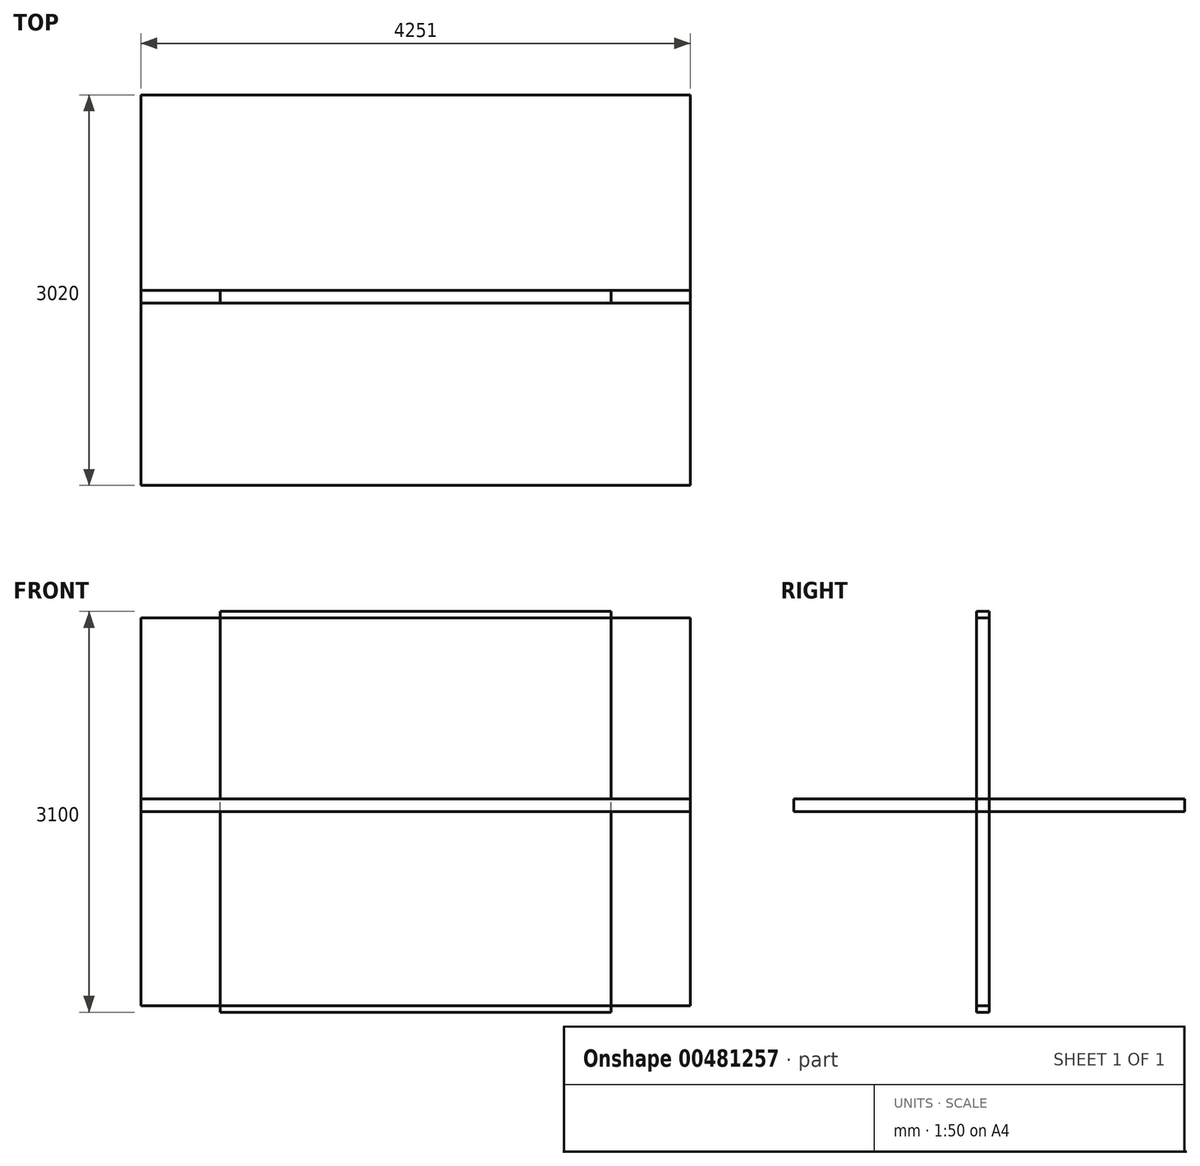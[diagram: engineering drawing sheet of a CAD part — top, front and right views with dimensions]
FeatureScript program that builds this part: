
annotation { "Feature Type Name" : "Feature", "Feature Type Description" : "" }
export const myFeature = defineFeature(function(context is Context, id is Id, definition is map)
    precondition{}
    {
        {
            var Q0;
            Q0=qCreatedBy(makeId("Front.planeOp"),FACE);
            var sketch = newSketch(context, id + "F0", { "sketchPlane" : qUnion([Q0])});
            skLineSegment(sketch, "E0.bottom", {"start": v(2125.5, -1500) * mm, "end": v(-2125.5, -1500) * mm});
            skLineSegment(sketch, "E0.top", {"start": v(2125.5, 1500) * mm, "end": v(-2125.5, 1500) * mm});
            skLineSegment(sketch, "E0.left", {"start": v(2125.5, -1500) * mm, "end": v(2125.5, 1500) * mm});
            skLineSegment(sketch, "E0.right", {"start": v(-2125.5, -1500) * mm, "end": v(-2125.5, 1500) * mm});
            skPoint(sketch, "E0.middle", {"position": v(0, 0) * mm});
            skSolve(sketch);
        }
        {
            var Q0;
            Q0 = qSketchRegion(id + "F0", true);
            extrude(context, id + "F1", {"entities" : qUnion([Q0]), "depth" : 100 * mm});
        }
        {
            var Q0;
            Q0=qCreatedBy(makeId("Top.planeOp"),FACE);
            var sketch = newSketch(context, id + "F2", { "sketchPlane" : qUnion([Q0])});
            skLineSegment(sketch, "E1.bottom", {"start": v(2125.5, -1510) * mm, "end": v(-2125.5, -1510) * mm});
            skLineSegment(sketch, "E1.top", {"start": v(2125.5, 1510) * mm, "end": v(-2125.5, 1510) * mm});
            skLineSegment(sketch, "E1.left", {"start": v(2125.5, -1510) * mm, "end": v(2125.5, 1510) * mm});
            skLineSegment(sketch, "E1.right", {"start": v(-2125.5, -1510) * mm, "end": v(-2125.5, 1510) * mm});
            skPoint(sketch, "E1.middle", {"position": v(0, 0) * mm});
            skSolve(sketch);
        }
        {
            var Q0;
            Q0 = qSketchRegion(id + "F2", true);
            extrude(context, id + "F3", {"entities" : qUnion([Q0]), "depth" : 100 * mm});
        }
        {
            var Q0;
            Q0=qCreatedBy(makeId("Front.planeOp"),FACE);
            var sketch = newSketch(context, id + "F4", { "sketchPlane" : qUnion([Q0])});
            skLineSegment(sketch, "E2.bottom", {"start": v(1510, -1550) * mm, "end": v(-1510, -1550) * mm});
            skLineSegment(sketch, "E2.top", {"start": v(1510, 1550) * mm, "end": v(-1510, 1550) * mm});
            skLineSegment(sketch, "E2.left", {"start": v(1510, -1550) * mm, "end": v(1510, 1550) * mm});
            skLineSegment(sketch, "E2.right", {"start": v(-1510, -1550) * mm, "end": v(-1510, 1550) * mm});
            skPoint(sketch, "E2.middle", {"position": v(0, 0) * mm});
            skSolve(sketch);
        }
        {
            var Q0;
            Q0 = qSketchRegion(id + "F4", true);
            extrude(context, id + "F5", {"entities" : qUnion([Q0]), "depth" : 100 * mm});
        }
    });
